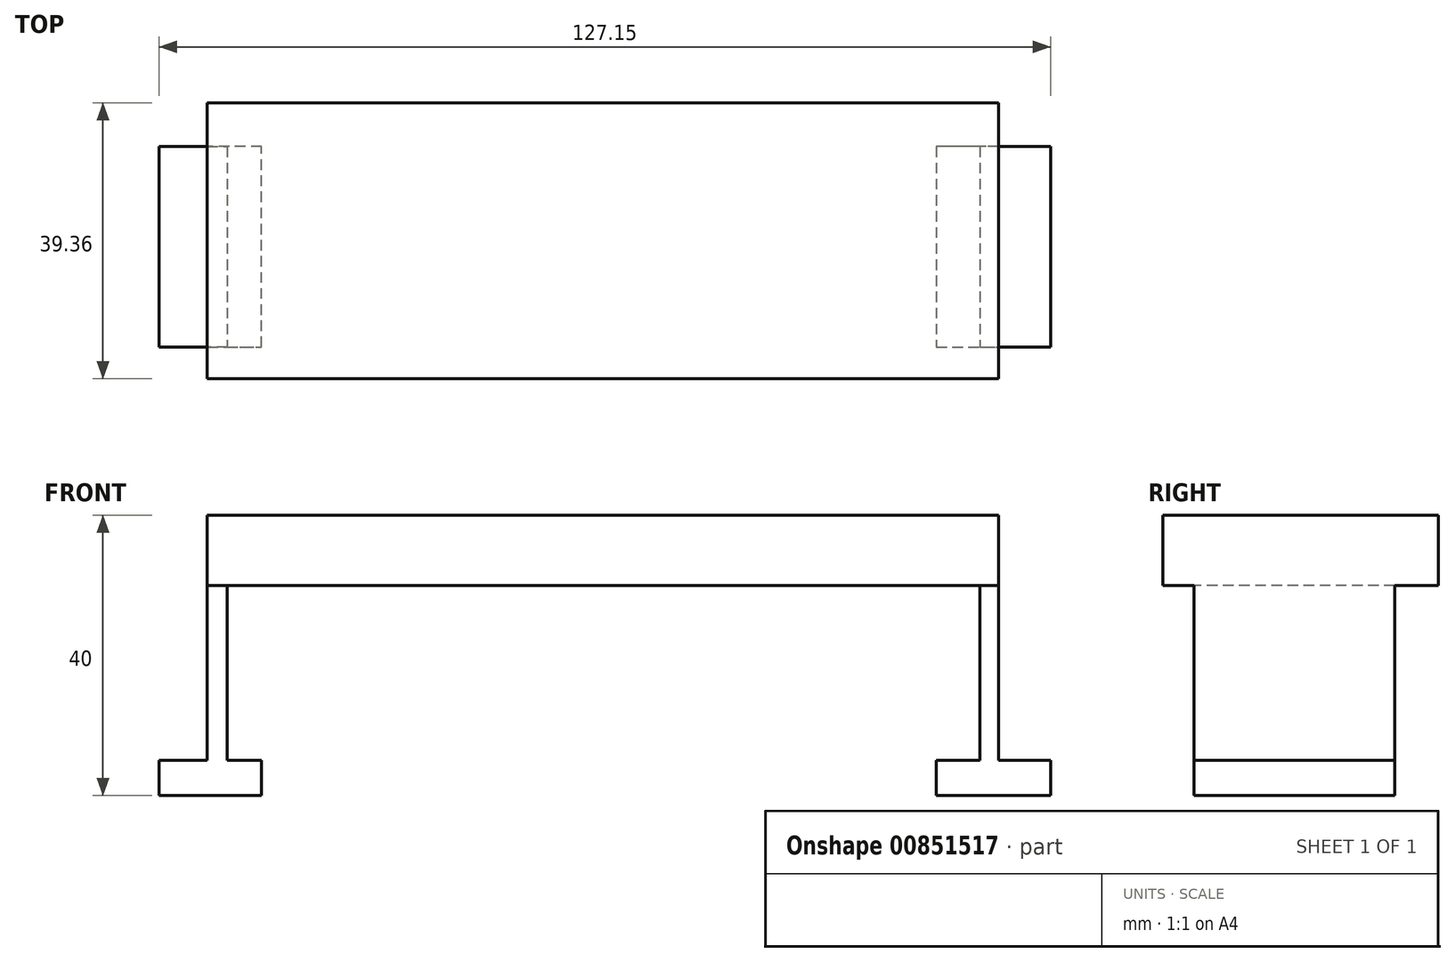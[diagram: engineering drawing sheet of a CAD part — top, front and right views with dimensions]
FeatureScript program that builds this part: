
annotation { "Feature Type Name" : "Feature", "Feature Type Description" : "" }
export const myFeature = defineFeature(function(context is Context, id is Id, definition is map)
    precondition{}
    {
        {
            var Q0;
            Q0=qCreatedBy(makeId("Top.planeOp"),FACE);
            var sketch = newSketch(context, id + "F0", { "sketchPlane" : qUnion([Q0])});
            skLineSegment(sketch, "E0", {"start": v(-54.84, 19.1) * mm, "end": v(-54.84, -20.26) * mm});
            skLineSegment(sketch, "E1", {"start": v(-54.84, -20.26) * mm, "end": v(58.02, -20.26) * mm});
            skLineSegment(sketch, "E2", {"start": v(58.02, -20.26) * mm, "end": v(58.02, 19.1) * mm});
            skLineSegment(sketch, "E3", {"start": v(58.02, 19.1) * mm, "end": v(-54.84, 19.1) * mm});
            skSolve(sketch);
        }
        {
            var Q0;
            Q0 = qSketchRegion(id + "F0", true);
            extrude(context, id + "F1", {"entities" : qUnion([Q0]), "depth" : 10 * mm, "offsetDistance" : 25 * mm});
        }
        {
            var Q0;
            Q0=makeQuery(id+"F1.opExtrude","CAP_FACE",FACE,{"disambiguationData":[OSD([sQuery(id+"F0.wireOp",EDGE,"E0"),sQuery(id+"F0.wireOp",EDGE,"E1"),sQuery(id+"F0.wireOp",EDGE,"E2"),sQuery(id+"F0.wireOp",EDGE,"E3")])],"isStart":true});
            var sketch = newSketch(context, id + "F2", { "sketchPlane" : qUnion([Q0])});
            skLineSegment(sketch, "E4", {"start": v(-54.84, 15.76) * mm, "end": v(-54.84, -12.86) * mm});
            skLineSegment(sketch, "E5", {"start": v(-54.84, -12.86) * mm, "end": v(-52, -12.86) * mm});
            skLineSegment(sketch, "E6", {"start": v(-52, -12.86) * mm, "end": v(-52, 15.76) * mm});
            skLineSegment(sketch, "E7", {"start": v(-52, 15.76) * mm, "end": v(-54.84, 15.76) * mm});
            skLineSegment(sketch, "E8", {"start": v(58.02, 15.76) * mm, "end": v(58.02, -12.86) * mm});
            skLineSegment(sketch, "E9", {"start": v(58.02, -12.86) * mm, "end": v(55.37, -12.86) * mm});
            skLineSegment(sketch, "E10", {"start": v(55.37, -12.86) * mm, "end": v(55.37, 15.76) * mm});
            skLineSegment(sketch, "E11", {"start": v(55.37, 15.76) * mm, "end": v(58.02, 15.76) * mm});
            skSolve(sketch);
        }
        {
            var Q0;
            Q0 = qSketchRegion(id + "F2", true);
            extrude(context, id + "F3", {"entities" : qUnion([Q0]), "operationType" : NewBodyOperationType.ADD, "depth" : 25 * mm, "offsetDistance" : 25 * mm});
        }
        {
            var Q0;
            Q0=makeQuery(id+"F3.opExtrude","CAP_FACE",FACE,{"disambiguationData":[OSD([sQuery(id+"F2.wireOp",EDGE,"E4"),sQuery(id+"F2.wireOp",EDGE,"E5"),sQuery(id+"F2.wireOp",EDGE,"E6"),sQuery(id+"F2.wireOp",EDGE,"E7")])],"isStart":false});
            var sketch = newSketch(context, id + "F4", { "sketchPlane" : qUnion([Q0])});
            skLineSegment(sketch, "E12", {"start": v(-61.71, 15.76) * mm, "end": v(-47.1, 15.76) * mm});
            skLineSegment(sketch, "E13", {"start": v(-47.1, 15.76) * mm, "end": v(-47.1, -12.86) * mm});
            skLineSegment(sketch, "E14", {"start": v(-47.1, -12.86) * mm, "end": v(-61.71, -12.86) * mm});
            skLineSegment(sketch, "E15", {"start": v(-61.71, -12.86) * mm, "end": v(-61.71, 15.76) * mm});
            skSolve(sketch);
        }
        {
            var Q0;
            Q0 = qSketchRegion(id + "F4", true);
            extrude(context, id + "F5", {"entities" : qUnion([Q0]), "operationType" : NewBodyOperationType.ADD, "depth" : 5 * mm, "offsetDistance" : 25 * mm});
        }
        {
            var Q0;
            Q0=makeQuery(id+"F3.opExtrude","CAP_FACE",FACE,{"disambiguationData":[OSD([sQuery(id+"F2.wireOp",EDGE,"E8"),sQuery(id+"F2.wireOp",EDGE,"E9"),sQuery(id+"F2.wireOp",EDGE,"E10"),sQuery(id+"F2.wireOp",EDGE,"E11")])],"isStart":false});
            var sketch = newSketch(context, id + "F6", { "sketchPlane" : qUnion([Q0])});
            skLineSegment(sketch, "E16", {"start": v(49.15, 15.76) * mm, "end": v(65.44, 15.76) * mm});
            skLineSegment(sketch, "E17", {"start": v(65.44, 15.76) * mm, "end": v(65.44, -12.86) * mm});
            skLineSegment(sketch, "E18", {"start": v(65.44, -12.86) * mm, "end": v(49.15, -12.86) * mm});
            skLineSegment(sketch, "E19", {"start": v(49.15, -12.86) * mm, "end": v(49.15, 15.76) * mm});
            skSolve(sketch);
        }
        {
            var Q0;
            Q0 = qSketchRegion(id + "F6", true);
            extrude(context, id + "F7", {"entities" : qUnion([Q0]), "operationType" : NewBodyOperationType.ADD, "depth" : 5 * mm, "offsetDistance" : 25 * mm});
        }
    });
